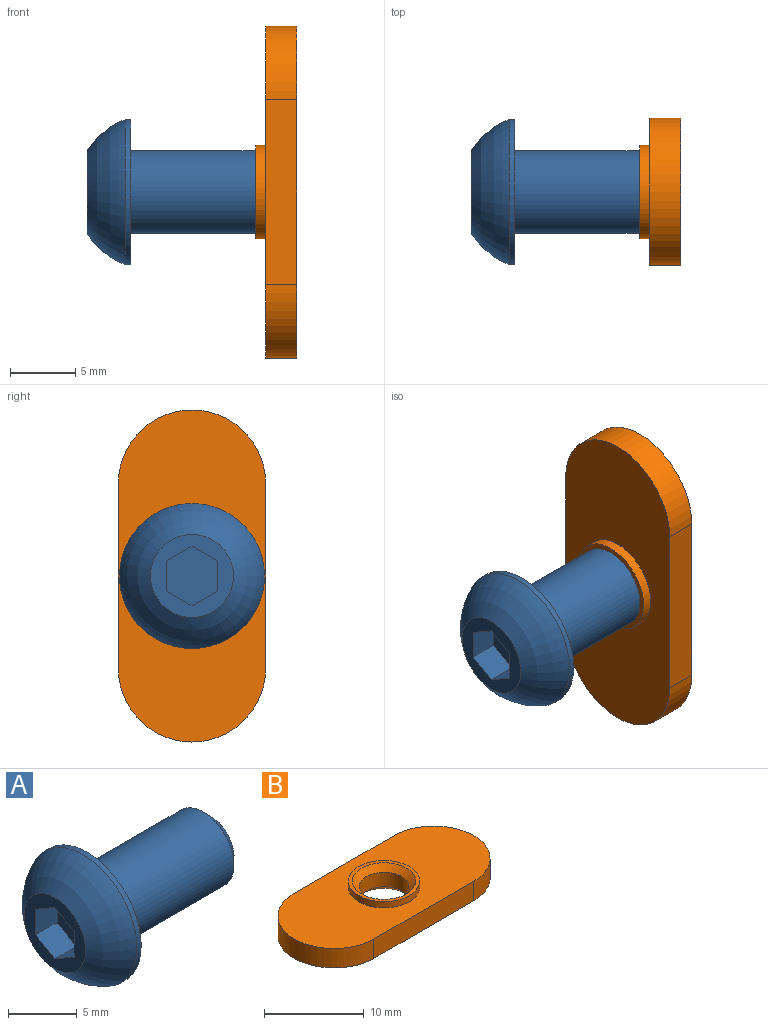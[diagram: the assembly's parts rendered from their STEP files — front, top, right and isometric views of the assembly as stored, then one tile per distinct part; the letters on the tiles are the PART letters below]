
ASSEMBLY  parts=2 mates=1
PART A: 14 faces, bbox 16.1x11.1x11.1 mm
  f0: plane 2.22x1.98mm, normal (0,-0.5,0.87), area 5.1mm2, adj f1,f2,f3,f13
  f1: plane 2.29x2.22mm, normal (0,-1,0), area 5.1mm2, adj f0,f3,f10,f13
  f2: plane 2.22x1.98mm, normal (0,0.5,0.87), area 5.1mm2, adj f0,f3,f12,f13
  f3: plane 6.35x6.35mm, normal (-1,0,0), area 18mm2, adj f0,f1,f2,f4,f10,f11,f12
  f4: torus R=0.01mm, axis (1,0,0), area 108.8mm2, adj f3,f5
  f5: cylinder r=5.55mm len=11.1mm, axis (-1,0,0), area 15.1mm2, adj f4,f6
  f6: plane 11.1x11.1mm, normal (1,0,0), area 65.1mm2, adj f5,f7
  f7: cylinder r=3.17mm len=11.94mm, axis (-1,0,0), area 238.3mm2, adj f6,f8
  f8: cone r=3.17mm half-angle=45deg, axis (-1,0,0), area 18.8mm2, adj f7,f9
  f9: plane 4.84x4.84mm, normal (1,0,0), area 18.4mm2, adj f8
  f10: plane 2.22x1.98mm, normal (0,-0.5,-0.87), area 5.1mm2, adj f1,f3,f11,f13
  f11: plane 2.22x1.98mm, normal (0,0.5,-0.87), area 5.1mm2, adj f3,f10,f12,f13
  f12: plane 2.29x2.22mm, normal (0,1,0), area 5.1mm2, adj f2,f3,f11,f13
  f13: plane 4.58x3.97mm, normal (-1,0,0), area 13.6mm2, adj f0,f1,f2,f10,f11,f12
PART B: 11 faces, bbox 25.4x11.3x3.1 mm
  f0: plane 25.4x11.25mm, normal (0,0,-1), area 227mm2, adj f3,f4,f5,f6,f10
  f1: cylinder r=3.57mm len=7.14mm, axis (0,0,1), area 17.1mm2, adj f2,f7
  f2: plane 25.4x11.25mm, normal (0,0,1), area 218.6mm2, adj f1,f3,f4,f5,f6
  f3: plane 14.15x2.39mm, normal (0,1,0), area 33.8mm2, adj f0,f2,f4,f6
  f4: cylinder r=5.63mm len=11.25mm, axis (0,0,1), area 42.2mm2, adj f0,f2,f3,f5
  f5: plane 14.15x2.39mm, normal (0,-1,0), area 33.8mm2, adj f0,f2,f4,f6
  f6: cylinder r=5.63mm len=11.25mm, axis (0,0,1), area 42.2mm2, adj f0,f2,f3,f5
  f7: plane 7.14x7.14mm, normal (0,0,1), area 8.3mm2, adj f1,f8
  f8: cone r=3.17mm half-angle=45deg, axis (0,0,1), area 17.3mm2, adj f7,f9
  f9: cylinder r=2.49mm len=4.98mm, axis (0,0,1), area 27.8mm2, adj f8,f10
  f10: cone r=2.49mm half-angle=45deg, axis (0,0,-1), area 17.3mm2, adj f0,f9
PLACE A t=(12.24,14.49,-6.61)mm
PLACE B rot(axis=(0,-1,0),90deg) t=(23.75,14.49,-6.61)mm
MATE fastened B.f1 <-> A.f5  axis (1,0,0) through (24.94,14.49,-6.61)mm
